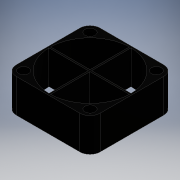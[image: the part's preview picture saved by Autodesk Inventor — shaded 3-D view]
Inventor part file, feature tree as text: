
AUTODESK INVENTOR PART (.ipt)
format: ipt  version: 2016 (Build 200138000, 138)  size: 159,744 bytes
history: native  units: mm
features: sketch x4, extrude x3, hole x1, fillet x1
ambient origin geometry x8: Origin, YZ Plane, XZ Plane, XY Plane, X Axis, Y Axis, Z Axis, Center Point
bodies: Solid1 (feature_tree)
feature tree (9):
  extrude  "Extrusion1"  Depth=25.0mm
  hole  "Hole1"  [1 undecoded]
  fillet  "Fillet1"  [1 undecoded]
  extrude  "Extrusion2"  Depth=3.0mm
  extrude  "Extrusion3"  Depth=10.0mm
  sketch  "Sketch1"  dims[d0=25.0mm d1=25.0mm]
  sketch  "Sketch2"  dims[d2=10.0mm d3=0.0mm d4=28.0mm d5=45.0deg]
  sketch  "Sketch3"  dims[d6=40.0mm d8=360.0deg]
  sketch  "Sketch4"  dims[d10=3.0mm d11=6.0mm d12=4.0mm d13=2.0mm d14=90.0deg d15=15.25mm d16=20.594885mm d17=3.0mm d18=24.0mm d19=10.0mm d20=0.0mm d21=0.5mm d22=0.5mm d23=10.0mm d24=0.0mm]
note: 2 required parameter values undecoded (feature->parameter linkage not recoverable at this tier; creation-order binding heuristic only, values carry confidence <= 0.55)
